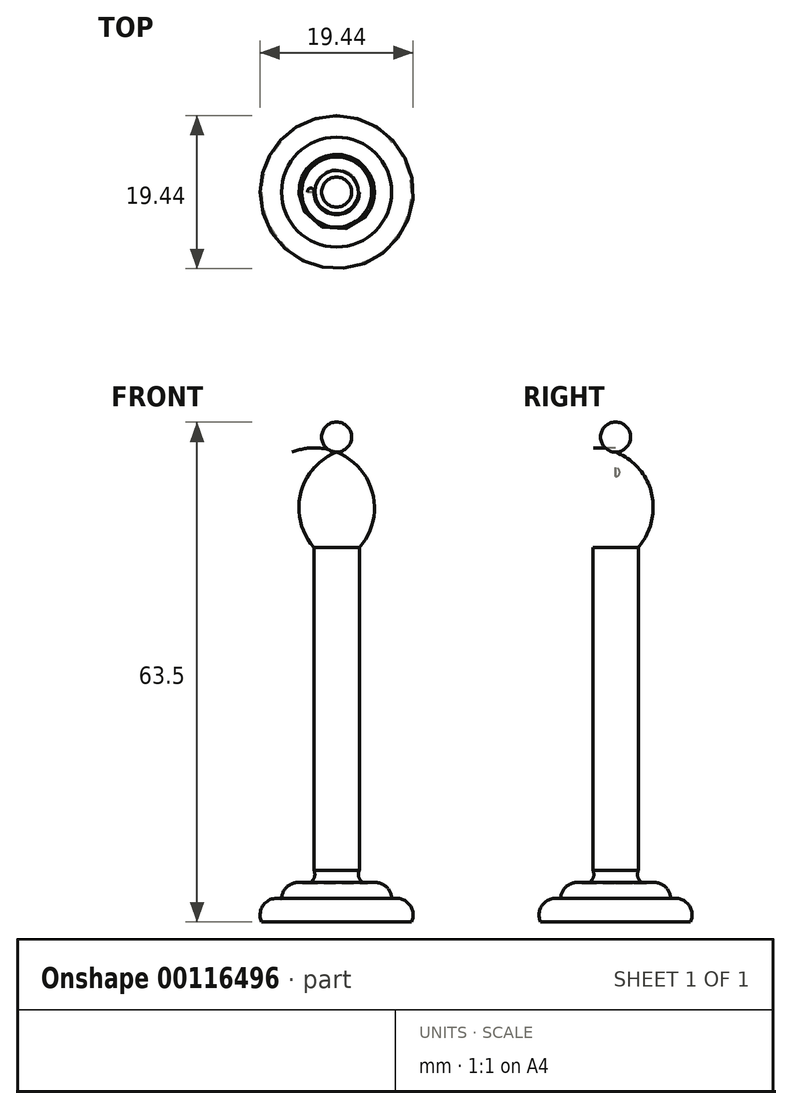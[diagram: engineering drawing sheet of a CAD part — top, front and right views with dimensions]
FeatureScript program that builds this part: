
annotation { "Feature Type Name" : "Feature", "Feature Type Description" : "" }
export const myFeature = defineFeature(function(context is Context, id is Id, definition is map)
    precondition{}
    {
        {
            var Q0;
            Q0=qCreatedBy(makeId("Front.planeOp"),FACE);
            var sketch = newSketch(context, id + "F0", { "sketchPlane" : qUnion([Q0])});
            skLineSegment(sketch, "E0", {"start": v(0, 0) * mm, "end": v(0, 63.5) * mm});
            skLineSegment(sketch, "E1", {"start": v(0, 0) * mm, "end": v(-9.53, 0) * mm});
            skArc(sketch, "E2", {"start": v(-6.99, 2.91) * mm, "mid": v(-9.2, 2.28) * mm, "end": v(-9.53, 0) * mm});
            skArc(sketch, "E3", {"start": v(-4.44, 4.99) * mm, "mid": v(-6.2, 4.55) * mm, "end": v(-6.99, 2.91) * mm});
            skArc(sketch, "E4", {"start": v(0, 63.5) * mm, "mid": v(-1.9, 61.6) * mm, "end": v(0, 59.69) * mm});
            skArc(sketch, "E5", {"start": v(0, 59.69) * mm, "mid": v(-4.6, 54.37) * mm, "end": v(-2.88, 47.56) * mm});
            skArc(sketch, "E6", {"start": v(-4.44, 4.99) * mm, "mid": v(-3.11, 5.2) * mm, "end": v(-2.88, 6.54) * mm});
            skLineSegment(sketch, "E7", {"start": v(-2.88, 6.54) * mm, "end": v(-2.88, 47.56) * mm});
            skPoint(sketch, "E8.end.orphan", {"position": v(-4.44, 0) * mm});
            skPoint(sketch, "E9.end.orphan", {"position": v(-6.99, 0) * mm});
            skSolve(sketch);
        }
        {
            var Q0;
            Q0 = qSketchRegion(id + "F0", true);
            var Q1;
            Q1=sQuery(id+"F0.wireOp",EDGE,"E0");
            revolve(context, id + "F1", {"entities" : qUnion([Q0]), "axis" : qUnion([Q1]), "revolveType" : RevolveType.FULL});
        }
        {
            var Q0;
            Q0=qCreatedBy(makeId("Front.planeOp"),FACE);
            var sketch = newSketch(context, id + "F2", { "sketchPlane" : qUnion([Q0])});
            skLineSegment(sketch, "E10", {"start": v(-3.04, 58.09) * mm, "end": v(-1.9, 55.82) * mm});
            skLineSegment(sketch, "E11", {"start": v(-4.17, 57.52) * mm, "end": v(-3.04, 58.09) * mm});
            skLineSegment(sketch, "E12", {"start": v(-1.9, 55.82) * mm, "end": v(-3.04, 55.25) * mm});
            skLineSegment(sketch, "E13", {"start": v(-4.17, 57.52) * mm, "end": v(-3.04, 55.25) * mm});
            skSolve(sketch);
        }
        {
            var Q0;
            Q0 = qSketchRegion(id + "F2", true);
            extrude(context, id + "F3", {"entities" : qUnion([Q0]), "operationType" : NewBodyOperationType.REMOVE, "endBound" : BoundingType.THROUGH_ALL, "depth" : 25.4 * mm});
        }
        {
            var Q0;
            Q0=makeQuery(id+"F3.boolean.opBoolean","COPY",FACE,{"derivedFrom":makeQuery(id+"F3.opExtrude","CAP_FACE",FACE,{"disambiguationData":[OSD([sQuery(id+"F2.wireOp",EDGE,"E10"),sQuery(id+"F2.wireOp",EDGE,"E11"),sQuery(id+"F2.wireOp",EDGE,"E12"),sQuery(id+"F2.wireOp",EDGE,"E13")])],"isStart":true})});
            var sketch = newSketch(context, id + "F4", { "sketchPlane" : qUnion([Q0])});
            skLineSegment(sketch, "E14", {"start": v(-1.9, 55.82) * mm, "end": v(-3.04, 55.25) * mm});
            skLineSegment(sketch, "E15", {"start": v(-3.04, 55.25) * mm, "end": v(-3.7, 56.56) * mm});
            skLineSegment(sketch, "E16", {"start": v(-3.7, 56.56) * mm, "end": v(-2.84, 57.7) * mm});
            skLineSegment(sketch, "E17", {"start": v(-2.84, 57.7) * mm, "end": v(-1.9, 55.82) * mm});
            skSolve(sketch);
        }
        {
            var Q0;
            Q0 = qSketchRegion(id + "F4", true);
            extrude(context, id + "F5", {"entities" : qUnion([Q0]), "operationType" : NewBodyOperationType.REMOVE, "oppositeDirection" : true, "depth" : 25.4 * mm});
        }
    });
